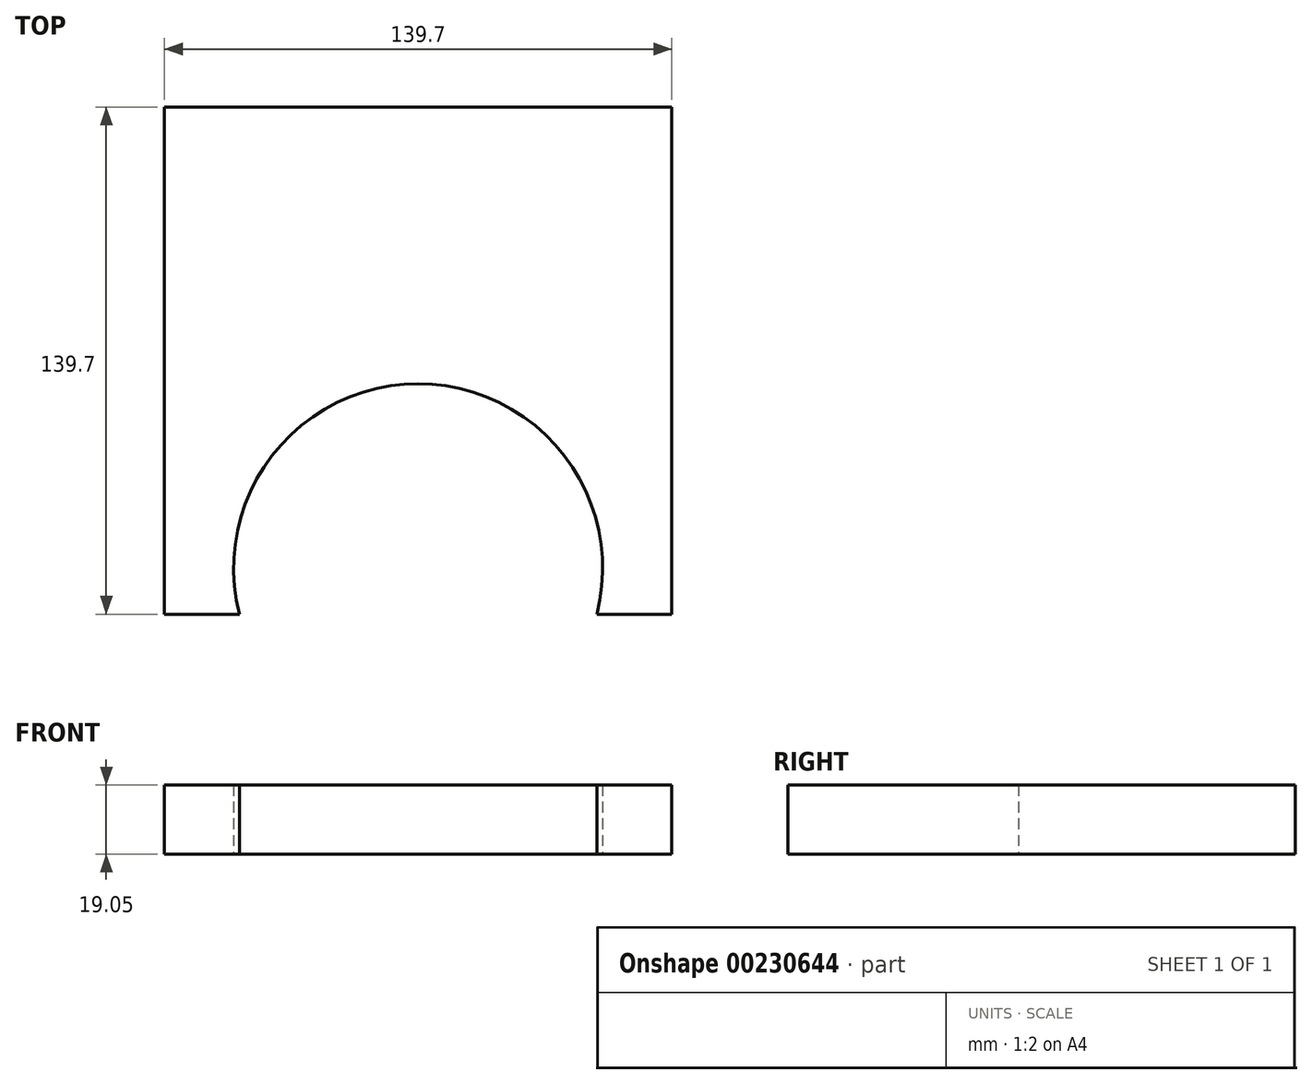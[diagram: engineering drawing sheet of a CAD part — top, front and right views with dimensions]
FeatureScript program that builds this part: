
annotation { "Feature Type Name" : "Feature", "Feature Type Description" : "" }
export const myFeature = defineFeature(function(context is Context, id is Id, definition is map)
    precondition{}
    {
        {
            var Q0;
            Q0=qCreatedBy(makeId("Top.planeOp"),FACE);
            var sketch = newSketch(context, id + "F0", { "sketchPlane" : qUnion([Q0])});
            skLineSegment(sketch, "E0.bottom", {"start": v(69.85, 69.85) * mm, "end": v(-69.85, 69.85) * mm});
            skLineSegment(sketch, "E0.top", {"start": v(69.85, -69.85) * mm, "end": v(-69.85, -69.85) * mm});
            skLineSegment(sketch, "E0.left", {"start": v(69.85, 69.85) * mm, "end": v(69.85, -69.85) * mm});
            skLineSegment(sketch, "E0.right", {"start": v(-69.85, 69.85) * mm, "end": v(-69.85, -69.85) * mm});
            skPoint(sketch, "E0.middle", {"position": v(0, 0) * mm});
            skLineSegment(sketch, "E1", {"start": v(0, -69.85) * mm, "end": v(0, -57.15) * mm});
            skPoint(sketch, "E1.endSnap0", {"position": v(0, -69.85) * mm});
            skArc(sketch, "E2", {"start": v(49.19, -69.85) * mm, "mid": v(0, -6.35) * mm, "end": v(-49.19, -69.85) * mm});
            skSolve(sketch);
        }
        {
            var Q0;
            Q0=makeQuery(id+"F0.imprint","IMPRINT",FACE,{"disambiguationData":[TD([[makeQuery(id+"F0.imprint","IMPRINT",EDGE,{"derivedFrom":sQuery(id+"F0.wireOp",EDGE,"E0.bottom")}),1.0]])]});
            extrude(context, id + "F1", {"entities" : qUnion([Q0]), "depth" : 19.05 * mm});
        }
    });
